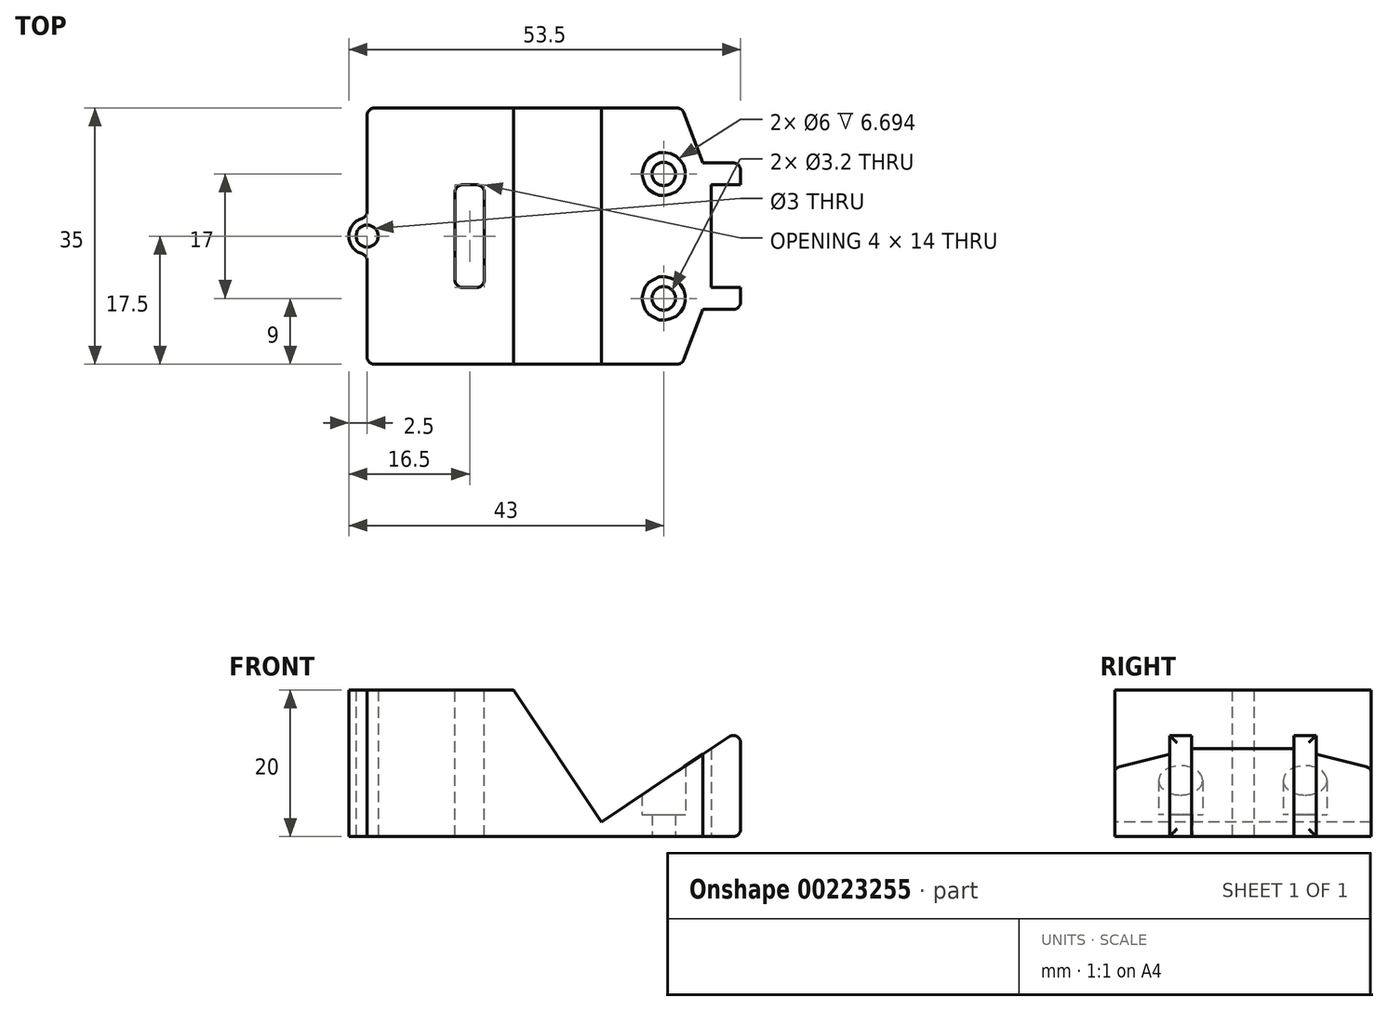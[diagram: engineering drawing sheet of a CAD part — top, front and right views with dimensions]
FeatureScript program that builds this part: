
annotation { "Feature Type Name" : "Feature", "Feature Type Description" : "" }
export const myFeature = defineFeature(function(context is Context, id is Id, definition is map)
    precondition{}
    {
        {
            var Q0;
            Q0=qCreatedBy(makeId("Top.planeOp"),FACE);
            var sketch = newSketch(context, id + "F0", { "sketchPlane" : qUnion([Q0])});
            skLineSegment(sketch, "E0.bottom", {"start": v(0, 0) * mm, "end": v(42.31, 0) * mm});
            skLineSegment(sketch, "E0.top", {"start": v(0, 35) * mm, "end": v(42.31, 35) * mm});
            skLineSegment(sketch, "E0.left", {"start": v(0, 0) * mm, "end": v(0, 15) * mm});
            skLineSegment(sketch, "E0.right", {"start": v(47, 10.68) * mm, "end": v(47, 24.32) * mm});
            skArc(sketch, "E1", {"start": v(0, 20) * mm, "mid": v(-2.5, 17.5) * mm, "end": v(0, 15) * mm});
            skCircle(sketch, "E2", {"center": v(0, 17.5) * mm, "radius": 1.5 * mm});
            skCircle(sketch, "E3", {"center": v(40.5, 26) * mm, "radius": 3 * mm});
            skCircle(sketch, "E4", {"center": v(40.5, 9) * mm, "radius": 3 * mm});
            skLineSegment(sketch, "E5", {"start": v(43.25, 0.64) * mm, "end": v(46.93, 10.33) * mm});
            skLineSegment(sketch, "E6", {"start": v(43.25, 34.36) * mm, "end": v(46.93, 24.67) * mm});
            skLineSegment(sketch, "E7.trimOffspring", {"start": v(0, 20) * mm, "end": v(0, 35) * mm});
            skPoint(sketch, "E8.visualSharp", {"position": v(43, 35) * mm});
            skArc(sketch, "E8.filletArc", {"start": v(43.25, 34.36) * mm, "mid": v(42.88, 34.82) * mm, "end": v(42.31, 35) * mm});
            skPoint(sketch, "E9.visualSharp", {"position": v(47, 24.5) * mm});
            skArc(sketch, "E9.filletArc", {"start": v(47, 24.32) * mm, "mid": v(46.98, 24.5) * mm, "end": v(46.93, 24.67) * mm});
            skPoint(sketch, "E10.visualSharp", {"position": v(47, 10.5) * mm});
            skArc(sketch, "E10.filletArc", {"start": v(46.93, 10.33) * mm, "mid": v(46.98, 10.5) * mm, "end": v(47, 10.68) * mm});
            skPoint(sketch, "E11.visualSharp", {"position": v(43, 0) * mm});
            skArc(sketch, "E11.filletArc", {"start": v(42.31, 0) * mm, "mid": v(42.88, 0.18) * mm, "end": v(43.25, 0.64) * mm});
            skSolve(sketch);
        }
        {
            var Q0;
            Q0=makeQuery(id+"F0.imprint","IMPRINT",FACE,{"disambiguationData":[TD([[makeQuery(id+"F0.imprint","IMPRINT",EDGE,{"derivedFrom":sQuery(id+"F0.wireOp",EDGE,"E0.bottom")}),1.0]])]});
            extrude(context, id + "F1", {"entities" : qUnion([Q0]), "depth" : 20 * mm});
        }
        {
            var Q0;
            Q0=makeQuery(id+"F1.opExtrude","SWEPT_FACE",FACE,{"disambiguationData":[OSD([sQuery(id+"F0.wireOp",EDGE,"E0.bottom")])]});
            var sketch = newSketch(context, id + "F2", { "sketchPlane" : qUnion([Q0])});
            skLineSegment(sketch, "E12.0", {"start": v(0, 20) * mm, "end": v(42.31, 20) * mm});
            skLineSegment(sketch, "E13.0", {"start": v(42.31, 20) * mm, "end": v(43.25, 20) * mm});
            skLineSegment(sketch, "E13.1", {"start": v(43.25, 20) * mm, "end": v(46.93, 20) * mm});
            skLineSegment(sketch, "E13.2", {"start": v(46.93, 20) * mm, "end": v(47, 20) * mm});
            skLineSegment(sketch, "E14.0", {"start": v(47, 20) * mm, "end": v(47, 0) * mm});
            skLineSegment(sketch, "E15", {"start": v(20, 20) * mm, "end": v(32, 2) * mm});
            skLineSegment(sketch, "E16", {"start": v(32, 2) * mm, "end": v(47, 12) * mm});
            skSolve(sketch);
        }
        {
            var Q0;
            Q0 = qSketchRegion(id + "F2", true);
            extrude(context, id + "F3", {"entities" : qUnion([Q0]), "operationType" : NewBodyOperationType.REMOVE, "endBound" : BoundingType.THROUGH_ALL, "oppositeDirection" : true, "depth" : 25 * mm});
        }
        {
            var Q0;
            Q0=makeQuery(id+"F1.opExtrude","CAP_FACE",FACE,{"disambiguationData":[OSD([sQuery(id+"F0.wireOp",EDGE,"E0.bottom"),sQuery(id+"F0.wireOp",EDGE,"E0.top"),sQuery(id+"F0.wireOp",EDGE,"E0.left"),sQuery(id+"F0.wireOp",EDGE,"E0.right"),sQuery(id+"F0.wireOp",EDGE,"E1"),sQuery(id+"F0.wireOp",EDGE,"E2"),sQuery(id+"F0.wireOp",EDGE,"E3"),sQuery(id+"F0.wireOp",EDGE,"E4"),sQuery(id+"F0.wireOp",EDGE,"E5"),sQuery(id+"F0.wireOp",EDGE,"E6"),sQuery(id+"F0.wireOp",EDGE,"E7.trimOffspring")])],"isStart":false});
            var sketch = newSketch(context, id + "F4", { "sketchPlane" : qUnion([Q0])});
            skLineSegment(sketch, "E17.bottom", {"start": v(13, 24.5) * mm, "end": v(15, 24.5) * mm});
            skLineSegment(sketch, "E17.top", {"start": v(13, 10.5) * mm, "end": v(15, 10.5) * mm});
            skLineSegment(sketch, "E17.left", {"start": v(12, 23.5) * mm, "end": v(12, 11.5) * mm});
            skLineSegment(sketch, "E17.right", {"start": v(16, 23.5) * mm, "end": v(16, 11.5) * mm});
            skCircle(sketch, "E18.0", {"center": v(0, 17.5) * mm, "radius": 1.5 * mm});
            skLineSegment(sketch, "E19", {"start": v(12, 17.5) * mm, "end": v(0, 17.5) * mm, "construction": true});
            skPoint(sketch, "E20.visualSharp", {"position": v(12, 24.5) * mm});
            skArc(sketch, "E20.filletArc", {"start": v(13, 24.5) * mm, "mid": v(12.3, 24.2) * mm, "end": v(12, 23.5) * mm});
            skPoint(sketch, "E21.visualSharp", {"position": v(16, 24.5) * mm});
            skArc(sketch, "E21.filletArc", {"start": v(16, 23.5) * mm, "mid": v(15.7, 24.2) * mm, "end": v(15, 24.5) * mm});
            skPoint(sketch, "E22.visualSharp", {"position": v(12, 10.5) * mm});
            skArc(sketch, "E22.filletArc", {"start": v(12, 11.5) * mm, "mid": v(12.3, 10.8) * mm, "end": v(13, 10.5) * mm});
            skPoint(sketch, "E23.visualSharp", {"position": v(16, 10.5) * mm});
            skArc(sketch, "E23.filletArc", {"start": v(15, 10.5) * mm, "mid": v(15.7, 10.8) * mm, "end": v(16, 11.5) * mm});
            skSolve(sketch);
        }
        {
            var Q0;
            Q0=makeQuery(id+"F1.opExtrude","CAP_FACE",FACE,{"disambiguationData":[OSD([sQuery(id+"F0.wireOp",EDGE,"E0.bottom"),sQuery(id+"F0.wireOp",EDGE,"E0.top"),sQuery(id+"F0.wireOp",EDGE,"E0.left"),sQuery(id+"F0.wireOp",EDGE,"E0.right"),sQuery(id+"F0.wireOp",EDGE,"E1"),sQuery(id+"F0.wireOp",EDGE,"E2"),sQuery(id+"F0.wireOp",EDGE,"E3"),sQuery(id+"F0.wireOp",EDGE,"E4"),sQuery(id+"F0.wireOp",EDGE,"E5"),sQuery(id+"F0.wireOp",EDGE,"E6"),sQuery(id+"F0.wireOp",EDGE,"E7.trimOffspring"),sQuery(id+"F0.wireOp",EDGE,"E8.filletArc"),sQuery(id+"F0.wireOp",EDGE,"E9.filletArc"),sQuery(id+"F0.wireOp",EDGE,"E10.filletArc"),sQuery(id+"F0.wireOp",EDGE,"E11.filletArc")])],"isStart":true});
            var sketch = newSketch(context, id + "F5", { "sketchPlane" : qUnion([Q0])});
            skCircle(sketch, "E24.0", {"center": v(40.5, -9) * mm, "radius": 3 * mm});
            skCircle(sketch, "E25.0", {"center": v(40.5, -26) * mm, "radius": 3 * mm});
            skCircle(sketch, "E26", {"center": v(40.5, -9) * mm, "radius": 1.6 * mm});
            skCircle(sketch, "E27", {"center": v(40.5, -26) * mm, "radius": 1.6 * mm});
            skSolve(sketch);
        }
        {
            var Q0;
            Q0=makeQuery(id+"F5.imprint","IMPRINT",FACE,{"disambiguationData":[TD([[makeQuery(id+"F5.imprint","IMPRINT",EDGE,{"derivedFrom":sQuery(id+"F5.wireOp",EDGE,"E24.0")}),-1.0]])]});
            var Q1;
            Q1=makeQuery(id+"F5.imprint","IMPRINT",FACE,{"disambiguationData":[TD([[makeQuery(id+"F5.imprint","IMPRINT",EDGE,{"derivedFrom":sQuery(id+"F5.wireOp",EDGE,"E25.0")}),-1.0]])]});
            extrude(context, id + "F6", {"entities" : qUnion([Q0, Q1]), "operationType" : NewBodyOperationType.ADD, "oppositeDirection" : true, "depth" : 3 * mm});
        }
        {
            var Q0;
            Q0=makeQuery(id+"F4.imprint","IMPRINT",FACE,{"disambiguationData":[TD([[makeQuery(id+"F4.imprint","IMPRINT",EDGE,{"derivedFrom":sQuery(id+"F4.wireOp",EDGE,"E17.bottom")}),-1.0]])]});
            extrude(context, id + "F7", {"entities" : qUnion([Q0]), "operationType" : NewBodyOperationType.REMOVE, "endBound" : BoundingType.THROUGH_ALL, "oppositeDirection" : true, "depth" : 25 * mm});
        }
        {
            var Q0;
            Q0=makeQuery(id+"F6.boolean.opBoolean","MERGE",FACE,{"derivedFrom":[makeQuery(id+"F1.opExtrude","CAP_FACE",FACE,{"disambiguationData":[OSD([sQuery(id+"F0.wireOp",EDGE,"E0.bottom"),sQuery(id+"F0.wireOp",EDGE,"E0.top"),sQuery(id+"F0.wireOp",EDGE,"E0.left"),sQuery(id+"F0.wireOp",EDGE,"E0.right"),sQuery(id+"F0.wireOp",EDGE,"E1"),sQuery(id+"F0.wireOp",EDGE,"E2"),sQuery(id+"F0.wireOp",EDGE,"E3"),sQuery(id+"F0.wireOp",EDGE,"E4"),sQuery(id+"F0.wireOp",EDGE,"E5"),sQuery(id+"F0.wireOp",EDGE,"E6"),sQuery(id+"F0.wireOp",EDGE,"E7.trimOffspring"),sQuery(id+"F0.wireOp",EDGE,"E8.filletArc"),sQuery(id+"F0.wireOp",EDGE,"E9.filletArc"),sQuery(id+"F0.wireOp",EDGE,"E10.filletArc"),sQuery(id+"F0.wireOp",EDGE,"E11.filletArc")])],"isStart":true}),makeQuery(id+"F6.opExtrude","CAP_FACE",FACE,{"disambiguationData":[OSD([sQuery(id+"F5.wireOp",EDGE,"E24.0"),sQuery(id+"F5.wireOp",EDGE,"E26")])],"isStart":true}),makeQuery(id+"F6.opExtrude","CAP_FACE",FACE,{"disambiguationData":[OSD([sQuery(id+"F5.wireOp",EDGE,"E25.0"),sQuery(id+"F5.wireOp",EDGE,"E27")])],"isStart":true})]});
            var sketch = newSketch(context, id + "F8", { "sketchPlane" : qUnion([Q0])});
            skLineSegment(sketch, "E28.bottom", {"start": v(45.86, -7.5) * mm, "end": v(51, -7.5) * mm});
            skLineSegment(sketch, "E28.top", {"start": v(46.98, -10.5) * mm, "end": v(51, -10.5) * mm});
            skLineSegment(sketch, "E28.right", {"start": v(51, -7.5) * mm, "end": v(51, -10.5) * mm});
            skLineSegment(sketch, "E29.bottom", {"start": v(45.86, -27.5) * mm, "end": v(51, -27.5) * mm});
            skLineSegment(sketch, "E29.top", {"start": v(46.98, -24.5) * mm, "end": v(51, -24.5) * mm});
            skLineSegment(sketch, "E29.right", {"start": v(51, -24.5) * mm, "end": v(51, -27.5) * mm});
            skLineSegment(sketch, "E30.0", {"start": v(16, -23.5) * mm, "end": v(16, -11.5) * mm});
            skLineSegment(sketch, "E31.0", {"start": v(12, -23.5) * mm, "end": v(12, -11.5) * mm});
            skLineSegment(sketch, "E32", {"start": v(12, -17.5) * mm, "end": v(16, -17.5) * mm});
            skLineSegment(sketch, "E33", {"start": v(51, -10.5) * mm, "end": v(51, -24.5) * mm});
            skLineSegment(sketch, "E34", {"start": v(51, -17.5) * mm, "end": v(16, -17.5) * mm, "construction": true});
            skLineSegment(sketch, "E35.0", {"start": v(43.25, -34.36) * mm, "end": v(46.93, -24.67) * mm});
            skLineSegment(sketch, "E36.0", {"start": v(47, -10.68) * mm, "end": v(47, -24.32) * mm});
            skLineSegment(sketch, "E37.0", {"start": v(43.25, -0.64) * mm, "end": v(46.93, -10.33) * mm});
            skArc(sketch, "E37.1", {"start": v(47, -24.32) * mm, "mid": v(46.98, -24.5) * mm, "end": v(46.93, -24.67) * mm});
            skArc(sketch, "E38.0", {"start": v(46.93, -10.33) * mm, "mid": v(46.98, -10.5) * mm, "end": v(47, -10.68) * mm});
            skSolve(sketch);
        }
        {
            var Q0;
            {var subQ3=sQuery(id+"F8.wireOp",EDGE,"E28.bottom");Q0=makeQuery(id+"F8.imprint","IMPRINT",FACE,{"disambiguationData":[TD([[makeQuery(id+"F8.imprint","IMPRINT",EDGE,{"derivedFrom":subQ3}),-1.0]])]});}
            var Q1;
            {var subQ3=sQuery(id+"F8.wireOp",EDGE,"E29.bottom");Q1=makeQuery(id+"F8.imprint","IMPRINT",FACE,{"disambiguationData":[TD([[makeQuery(id+"F8.imprint","IMPRINT",EDGE,{"derivedFrom":subQ3}),1.0]])]});}
            var Q2;
            Q2=makeQuery(id+"F3.boolean.opBoolean","COPY",FACE,{"derivedFrom":makeQuery(id+"F3.opExtrude","SWEPT_FACE",FACE,{"disambiguationData":[OSD([sQuery(id+"F2.wireOp",EDGE,"E16")])]})});
            var Q3;
            Q3=makeQuery(id+"F1.opExtrude","SWEPT_BODY",BODY,{"disambiguationData":[OSD([sQuery(id+"F0.wireOp",EDGE,"E0.bottom"),sQuery(id+"F0.wireOp",EDGE,"E0.top"),sQuery(id+"F0.wireOp",EDGE,"E0.left"),sQuery(id+"F0.wireOp",EDGE,"E0.right"),sQuery(id+"F0.wireOp",EDGE,"E1"),sQuery(id+"F0.wireOp",EDGE,"E2"),sQuery(id+"F0.wireOp",EDGE,"E3"),sQuery(id+"F0.wireOp",EDGE,"E4"),sQuery(id+"F0.wireOp",EDGE,"E5"),sQuery(id+"F0.wireOp",EDGE,"E6"),sQuery(id+"F0.wireOp",EDGE,"E7.trimOffspring"),sQuery(id+"F0.wireOp",EDGE,"E8.filletArc"),sQuery(id+"F0.wireOp",EDGE,"E9.filletArc"),sQuery(id+"F0.wireOp",EDGE,"E10.filletArc"),sQuery(id+"F0.wireOp",EDGE,"E11.filletArc")])]});
            extrude(context, id + "F9", {"entities" : qUnion([Q0, Q1]), "operationType" : NewBodyOperationType.ADD, "endBound" : BoundingType.UP_TO_SURFACE, "oppositeDirection" : true, "endBoundEntityFace" : qUnion([Q2]), "endBoundEntityBody" : qUnion([Q3]), "depth" : 15 * mm});
        }
        {
            var Q0;
            Q0=makeQuery(id+"F9.opExtrude","TWEAK_EDGE",EDGE,{"derivedFrom":[makeQuery(id+"F3.boolean.opBoolean","COPY",FACE,{"derivedFrom":makeQuery(id+"F3.opExtrude","SWEPT_FACE",FACE,{"disambiguationData":[OSD([sQuery(id+"F2.wireOp",EDGE,"pCvyz7Qj-ykgw-Gnc5-QEFr-8Be8TbLSWnNU")])]})}),makeQuery(id+"F8.imprint","IMPRINT",EDGE,{"derivedFrom":sQuery(id+"F8.wireOp",EDGE,"E28.right")})]});
            var Q1;
            Q1=makeQuery(id+"F9.opExtrude","TWEAK_EDGE",EDGE,{"derivedFrom":[makeQuery(id+"F3.boolean.opBoolean","COPY",FACE,{"derivedFrom":makeQuery(id+"F3.opExtrude","SWEPT_FACE",FACE,{"disambiguationData":[OSD([sQuery(id+"F2.wireOp",EDGE,"pCvyz7Qj-ykgw-Gnc5-QEFr-8Be8TbLSWnNU")])]})}),makeQuery(id+"F8.imprint","IMPRINT",EDGE,{"derivedFrom":sQuery(id+"F8.wireOp",EDGE,"E29.right")})]});
            var Q2;
            Q2=makeQuery(id+"F1.opExtrude","SWEPT_EDGE",EDGE,{"disambiguationData":[OSD([sQuery(id+"F0.wireOp",EDGE,"E0.bottom"),sQuery(id+"F0.wireOp",EDGE,"E0.left")])]});
            var Q3;
            Q3=makeQuery(id+"F1.opExtrude","SWEPT_EDGE",EDGE,{"disambiguationData":[OSD([sQuery(id+"F0.wireOp",EDGE,"E0.top"),sQuery(id+"F0.wireOp",EDGE,"E7.trimOffspring")])]});
            var Q4;
            Q4=makeQuery(id+"F1.opExtrude","SWEPT_EDGE",EDGE,{"disambiguationData":[OSD([sQuery(id+"F0.wireOp",EDGE,"E1"),sQuery(id+"F0.wireOp",EDGE,"E7.trimOffspring")])]});
            var Q5;
            Q5=makeQuery(id+"F1.opExtrude","SWEPT_EDGE",EDGE,{"disambiguationData":[OSD([sQuery(id+"F0.wireOp",EDGE,"E0.left"),sQuery(id+"F0.wireOp",EDGE,"E1")])]});
            var Q6;
            Q6=makeQuery(id+"F9.opExtrude","SWEPT_EDGE",EDGE,{"disambiguationData":[OSD([sQuery(id+"F8.wireOp",EDGE,"E28.bottom"),sQuery(id+"F8.wireOp",EDGE,"E37.0")])]});
            var Q7;
            Q7=makeQuery(id+"F9.opExtrude","SWEPT_EDGE",EDGE,{"disambiguationData":[OSD([sQuery(id+"F8.wireOp",EDGE,"E29.bottom"),sQuery(id+"F8.wireOp",EDGE,"E35.0")])]});
            var Q8;
            Q8=makeQuery(id+"F9.opExtrude","SWEPT_EDGE",EDGE,{"disambiguationData":[OSD([sQuery(id+"F8.wireOp",EDGE,"E28.bottom"),sQuery(id+"F8.wireOp",EDGE,"E28.right")])]});
            var Q9;
            Q9=makeQuery(id+"F9.opExtrude","SWEPT_EDGE",EDGE,{"disambiguationData":[OSD([sQuery(id+"F8.wireOp",EDGE,"E29.bottom"),sQuery(id+"F8.wireOp",EDGE,"E29.right")])]});
            var Q10;
            Q10=makeQuery(id+"F9.opExtrude","CAP_EDGE",EDGE,{"disambiguationData":[OSD([sQuery(id+"F8.wireOp",EDGE,"E28.right")])],"isStart":false});
            var Q11;
            Q11=makeQuery(id+"F9.opExtrude","CAP_EDGE",EDGE,{"disambiguationData":[OSD([sQuery(id+"F8.wireOp",EDGE,"E29.right")])],"isStart":false});
            var Q12;
            Q12=makeQuery(id+"F9.opExtrude","CAP_EDGE",EDGE,{"disambiguationData":[OSD([sQuery(id+"F8.wireOp",EDGE,"E28.right")])],"isStart":true});
            var Q13;
            Q13=makeQuery(id+"F9.opExtrude","CAP_EDGE",EDGE,{"disambiguationData":[OSD([sQuery(id+"F8.wireOp",EDGE,"E29.right")])],"isStart":true});
            fillet(context, id + "F10", {"entities" : qUnion([Q0, Q1, Q2, Q3, Q4, Q5, Q6, Q7, Q8, Q9, Q10, Q11, Q12, Q13]), "radius" : 1 * mm, "tangentPropagation" : true, "allowEdgeOverflow" : false});
        }
        {
            var Q0;
            Q0=makeQuery(id+"F1.opExtrude","SWEPT_BODY",BODY,{"disambiguationData":[OSD([sQuery(id+"F0.wireOp",EDGE,"E0.bottom"),sQuery(id+"F0.wireOp",EDGE,"E0.top"),sQuery(id+"F0.wireOp",EDGE,"E0.left"),sQuery(id+"F0.wireOp",EDGE,"E0.right"),sQuery(id+"F0.wireOp",EDGE,"E1"),sQuery(id+"F0.wireOp",EDGE,"E2"),sQuery(id+"F0.wireOp",EDGE,"E3"),sQuery(id+"F0.wireOp",EDGE,"E4"),sQuery(id+"F0.wireOp",EDGE,"E5"),sQuery(id+"F0.wireOp",EDGE,"E6"),sQuery(id+"F0.wireOp",EDGE,"E7.trimOffspring"),sQuery(id+"F0.wireOp",EDGE,"E8.filletArc"),sQuery(id+"F0.wireOp",EDGE,"E9.filletArc"),sQuery(id+"F0.wireOp",EDGE,"E10.filletArc"),sQuery(id+"F0.wireOp",EDGE,"E11.filletArc")])]});
            transform(context, id + "F11", {"entities" : qUnion([Q0]), "transformType" : TransformType.TRANSLATION_3D, "dx" : 0 * mm, "dy" : 0 * mm, "dz" : 0 * mm, "makeCopy" : true});
        }
        {
            var Q0;
            Q0=makeQuery(id+"F1.opExtrude","SWEPT_BODY",BODY,{"disambiguationData":[OSD([sQuery(id+"F0.wireOp",EDGE,"E0.bottom"),sQuery(id+"F0.wireOp",EDGE,"E0.top"),sQuery(id+"F0.wireOp",EDGE,"E0.left"),sQuery(id+"F0.wireOp",EDGE,"E0.right"),sQuery(id+"F0.wireOp",EDGE,"E1"),sQuery(id+"F0.wireOp",EDGE,"E2"),sQuery(id+"F0.wireOp",EDGE,"E3"),sQuery(id+"F0.wireOp",EDGE,"E4"),sQuery(id+"F0.wireOp",EDGE,"E5"),sQuery(id+"F0.wireOp",EDGE,"E6"),sQuery(id+"F0.wireOp",EDGE,"E7.trimOffspring"),sQuery(id+"F0.wireOp",EDGE,"E8.filletArc"),sQuery(id+"F0.wireOp",EDGE,"E9.filletArc"),sQuery(id+"F0.wireOp",EDGE,"E10.filletArc"),sQuery(id+"F0.wireOp",EDGE,"E11.filletArc")])]});
            deleteBodies(context, id + "F12", {"entities" : qUnion([Q0])});
        }
    });
